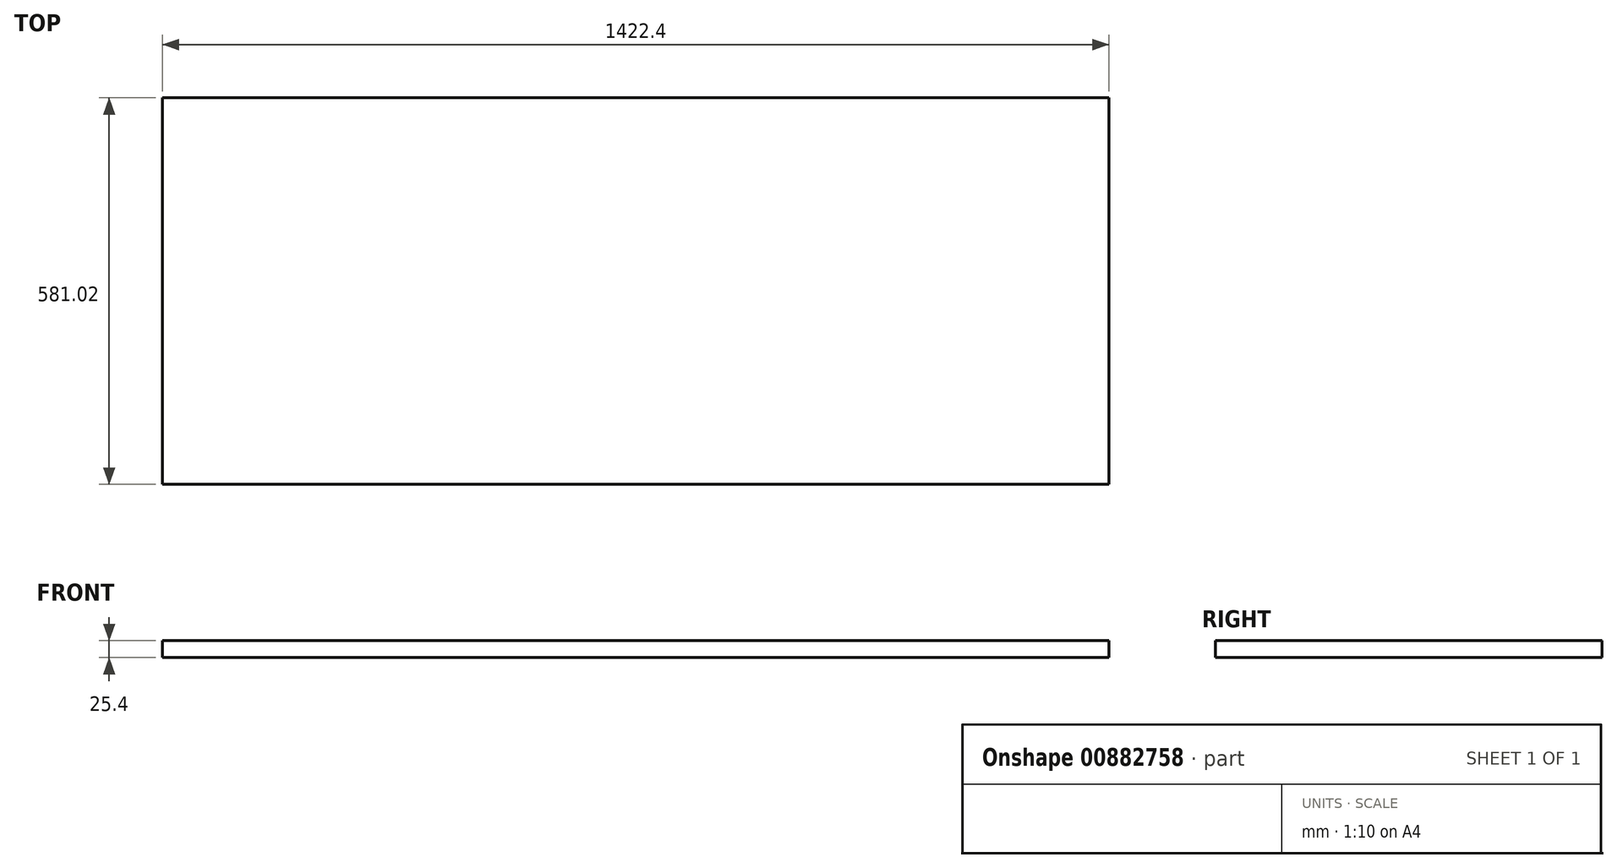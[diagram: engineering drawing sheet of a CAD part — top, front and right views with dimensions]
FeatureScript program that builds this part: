
annotation { "Feature Type Name" : "Feature", "Feature Type Description" : "" }
export const myFeature = defineFeature(function(context is Context, id is Id, definition is map)
    precondition{}
    {
        {
            var Q0;
            Q0=qCreatedBy(makeId("Front.planeOp"),FACE);
            var sketch = newSketch(context, id + "F0", { "sketchPlane" : qUnion([Q0])});
            skLineSegment(sketch, "E0.bottom", {"start": v(0, 0) * mm, "end": v(1422.4, 0) * mm});
            skLineSegment(sketch, "E0.top", {"start": v(0, 25.4) * mm, "end": v(1422.4, 25.4) * mm});
            skLineSegment(sketch, "E0.left", {"start": v(0, 0) * mm, "end": v(0, 25.4) * mm});
            skLineSegment(sketch, "E0.right", {"start": v(1422.4, 0) * mm, "end": v(1422.4, 25.4) * mm});
            skLineSegment(sketch, "E1.bottom", {"start": v(361.95, 0) * mm, "end": v(1060.45, 0) * mm});
            skLineSegment(sketch, "E1.top", {"start": v(361.95, -76.2) * mm, "end": v(1060.45, -76.2) * mm});
            skLineSegment(sketch, "E1.left", {"start": v(361.95, 0) * mm, "end": v(361.95, -76.2) * mm});
            skLineSegment(sketch, "E1.right", {"start": v(1060.45, 0) * mm, "end": v(1060.45, -76.2) * mm});
            skSolve(sketch);
        }
        {
            var Q0;
            Q0=makeQuery(id+"F0.imprint","IMPRINT",FACE,{"disambiguationData":[TD([[makeQuery(id+"F0.imprint","IMPRINT",EDGE,{"derivedFrom":sQuery(id+"F0.wireOp",EDGE,"E0.top")}),-1.0]])]});
            var Q1;
            Q1=makeQuery(id+"F0.imprint","IMPRINT",FACE,{"disambiguationData":[TD([[makeQuery(id+"F0.imprint","IMPRINT",EDGE,{"derivedFrom":sQuery(id+"F0.wireOp",EDGE,"E1.bottom")}),-1.0]])]});
            extrude(context, id + "F1", {"entities" : qUnion([Q0, Q1]), "depth" : 581.02 * mm, "offsetDistance" : 25.4 * mm});
        }
        {
            var Q0;
            Q0=makeQuery(id+"F1.opExtrude","CAP_FACE",FACE,{"disambiguationData":[OSD([sQuery(id+"F0.wireOp",EDGE,"E0.bottom"),sQuery(id+"F0.wireOp",EDGE,"E0.top"),sQuery(id+"F0.wireOp",EDGE,"E0.left"),sQuery(id+"F0.wireOp",EDGE,"E0.right"),sQuery(id+"F0.wireOp",EDGE,"E1.top"),sQuery(id+"F0.wireOp",EDGE,"E1.left"),sQuery(id+"F0.wireOp",EDGE,"E1.right")])],"isStart":false});
            var sketch = newSketch(context, id + "F2", { "sketchPlane" : qUnion([Q0])});
            skLineSegment(sketch, "E2.bottom", {"start": v(381, 0) * mm, "end": v(1041.4, 0) * mm});
            skLineSegment(sketch, "E2.top", {"start": v(381, -57.15) * mm, "end": v(1041.4, -57.15) * mm});
            skLineSegment(sketch, "E2.left", {"start": v(381, 0) * mm, "end": v(381, -57.15) * mm});
            skLineSegment(sketch, "E2.right", {"start": v(1041.4, 0) * mm, "end": v(1041.4, -57.15) * mm});
            skSolve(sketch);
        }
        {
            var Q0;
            Q0=makeQuery(id+"F2.imprint","IMPRINT",FACE,{"disambiguationData":[TD([[makeQuery(id+"F2.imprint","IMPRINT",EDGE,{"derivedFrom":sQuery(id+"F2.wireOp",EDGE,"E2.bottom")}),-1.0]])]});
            extrude(context, id + "F3", {"entities" : qUnion([Q0]), "operationType" : NewBodyOperationType.REMOVE, "oppositeDirection" : true, "depth" : 565.15 * mm, "offsetDistance" : 25.4 * mm});
        }
    });
